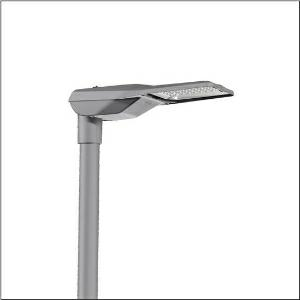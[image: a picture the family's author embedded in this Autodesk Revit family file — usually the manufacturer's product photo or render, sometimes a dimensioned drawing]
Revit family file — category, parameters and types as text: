
# Revit family: streetlight_sl_21_mini___pl52_5xe2h33s08gb_224a
name_source: partatom
category: Lighting Fixtures
units: mm (PartAtom-declared; Revit-internal decimal feet)

## family parameters
Cut with Voids When Loaded = No
Host = Face
Light Source = No
Part Type = Normal
Room Calculation Point = No
Round Connector Dimension = Use Diameter
Shared = No

## types (1)
- --- (1 x LED, 5840 lm, 40.4 W, 3000K)
    Apparent Load = 40 VA
    CIE Flux Codes = 27 59 98 100 100
    Color Rendering = 70
    Color Temperature = 3000K
    Default Elevation = 1800 mm
    Description = Streetlight SL 21 mini, mast luminaire, primary light control with lens, of PMMA, primary optical cover: cover, of toughened safety glass, transparent, light distribution: PL52, light emission: direct distribution, primary light characteristic: asymmetric, installation type: side-entry, post-top, LED, High Power LED, rated luminous flux: 5.840lm, luminous efficacy: 145lm/W, light colour: 730, colour temperature: 3000K, control gear: D4i, control: overheat protection, constant luminous flux control, time-dependent luminous flux control, flexible luminous flux parameterisation, pre-setting: logarithmic dimming characteristic, mains connection: 220..240V, AC, 50/60Hz, start of lifetime: 40W, end of service life: 41W, reduction: 19W, luminaire housing, of diecast aluminium, powder-coated, SITECO metallic grey (DB 702S), corrosivity category C5 high according to DIN EN ISO 12944, please order mast flange separately, inclination adjustable: 0°, 5°, 10°, 15°, sealing non-destructively replaceable, multi-level sealing system, length: 628mm, width: 235mm, height: 110mm, mast flange for spigot size: 42mm (side-entry): 5XC10008XM4, 60/48mm (side-entry/post-top): 5XC10108XM2, 76/60mm (side-entry/post-top): 5XC10108XM1, mounting height: 4..8m, Smart Interface above, protection rating (complete): IP66, insulation class (complete): insulation class II (safety insulation), certification: CE, ENEC, ENEC+, VDE, impact resistance: IK10, permissible operating ambient temperature for outdoor applications: -40..+50°C, standard-compliant lighting for roads and squares, packaging unit: 1 piece

Light Distribution: PL52
    Height = 110 mm
    Lamp = 1 x LED
    Lamp Light Flux = 5840 lm
    Lamp Power = 40.4 W
    Lamp count = 1
    Length = 625 mm
    Luminous efficacy = 145 lm/W
    Manufacturer = Siteco
    ModVariant = No
    Model = 5XE2H33S08GB
    Number of Poles = 1
    OnlyDefault = Yes
    Power Factor = 1
    Product Name = Streetlight SL 21 mini | PL52
    Product group = mast luminaire | pylon top
    ProductGroupID = 6100
    Protection Class = Protection class II
    Protection Degree = IP 66
    RLX_Detail_Level = 1
    RLX_Emergency_Light_Flux = 0 lm
    RLX_Emergency_Type = 0
    RLX_Emergency_Type_DB = No
    RlxData = <blob elided: 35721 chars, md5=273daa46>
    Socket = socket
    Standby Power = 0 W
    System Light Flux = 5840 lm
    System Power = 40 W
    Type Comments = factory setting: luminous flux: 100 % | dim-lin: 254 | 812 mA
    Type Image = l_1003515.jpg
    URL = http://relux.com
    VarID = @adj_187669
    Voltage = 0 V
    Weight = 0.00 kg
    Width = 234 mm

## geometry (parser evidence)
native form markers: Blend x4, Sweep x8
no freeform markers — native parametric forms only
